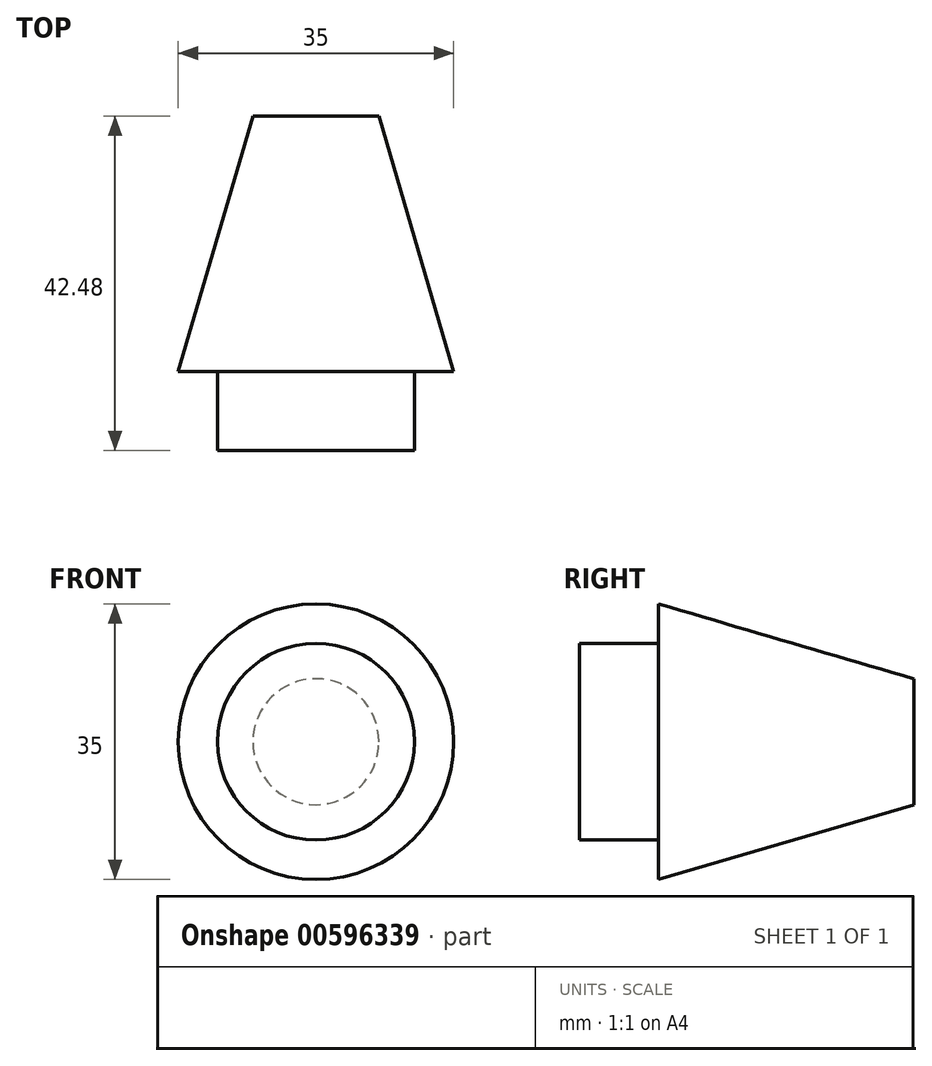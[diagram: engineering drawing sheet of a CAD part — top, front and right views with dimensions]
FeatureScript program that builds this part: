
annotation { "Feature Type Name" : "Feature", "Feature Type Description" : "" }
export const myFeature = defineFeature(function(context is Context, id is Id, definition is map)
    precondition{}
    {
        {
            var Q0;
            Q0=qCreatedBy(makeId("Top.planeOp"),FACE);
            var sketch = newSketch(context, id + "F0", { "sketchPlane" : qUnion([Q0])});
            skLineSegment(sketch, "E0", {"start": v(0, 42.48) * mm, "end": v(8, 42.48) * mm});
            skLineSegment(sketch, "E1", {"start": v(0, 0) * mm, "end": v(12.5, 0) * mm});
            skLineSegment(sketch, "E2", {"start": v(12.5, 0) * mm, "end": v(12.5, 10) * mm});
            skLineSegment(sketch, "E3", {"start": v(12.5, 10) * mm, "end": v(17.5, 10) * mm});
            skLineSegment(sketch, "E4", {"start": v(17.5, 10) * mm, "end": v(8, 42.48) * mm});
            skLineSegment(sketch, "E5", {"start": v(0, 42.48) * mm, "end": v(0, 0) * mm});
            skPoint(sketch, "E6.orphan", {"position": v(-8, 42.48) * mm});
            skPoint(sketch, "E7.orphan", {"position": v(-12.5, 0) * mm});
            skSolve(sketch);
        }
        {
            var Q0;
            Q0=makeQuery(id+"F0.imprint","IMPRINT",FACE,{"disambiguationData":[TD([[makeQuery(id+"F0.imprint","IMPRINT",EDGE,{"derivedFrom":sQuery(id+"F0.wireOp",EDGE,"E0")}),-1.0]])]});
            var Q1;
            Q1=sQuery(id+"F0.wireOp",EDGE,"E5");
            revolve(context, id + "F1", {"surfaceOperationType" : NewSurfaceOperationType.NEW, "entities" : qUnion([Q0]), "axis" : qUnion([Q1]), "revolveType" : RevolveType.FULL});
        }
    });
